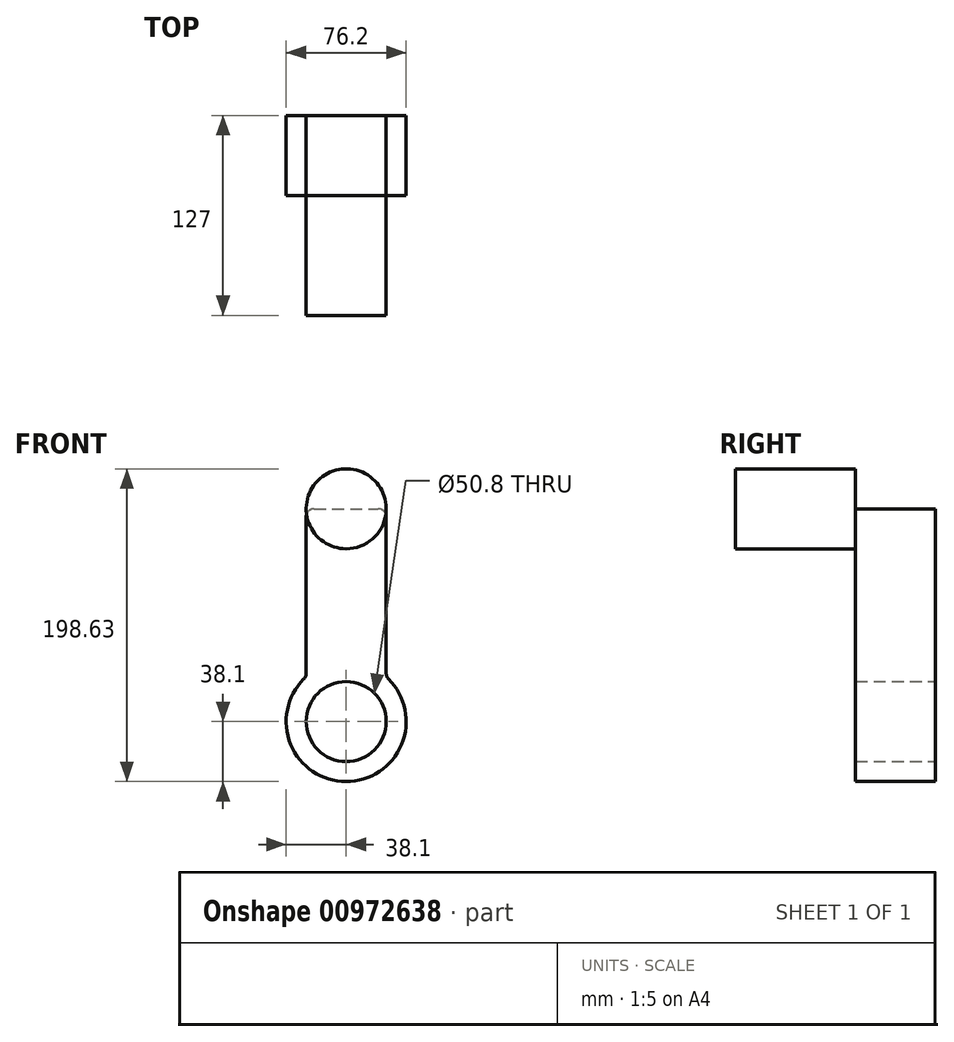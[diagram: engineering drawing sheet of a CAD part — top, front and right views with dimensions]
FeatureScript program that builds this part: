
annotation { "Feature Type Name" : "Feature", "Feature Type Description" : "" }
export const myFeature = defineFeature(function(context is Context, id is Id, definition is map)
    precondition{}
    {
        {
            var Q0;
            Q0=qCreatedBy(makeId("Front.planeOp"),FACE);
            var sketch = newSketch(context, id + "F0", { "sketchPlane" : qUnion([Q0])});
            skCircle(sketch, "E0", {"center": v(0, 0) * mm, "radius": 25.4 * mm});
            skCircle(sketch, "E1", {"center": v(0, 0) * mm, "radius": 38.1 * mm});
            skLineSegment(sketch, "E2.bottom", {"start": v(-18.1, 33.53) * mm, "end": v(18.4, 33.53) * mm});
            skLineSegment(sketch, "E2.top", {"start": v(-18.1, 135.13) * mm, "end": v(18.4, 135.13) * mm});
            skLineSegment(sketch, "E2.left", {"start": v(-18.1, 33.53) * mm, "end": v(-18.1, 135.13) * mm});
            skLineSegment(sketch, "E2.right", {"start": v(18.4, 33.53) * mm, "end": v(18.4, 135.13) * mm});
            skCircle(sketch, "E3", {"center": v(0, 135.13) * mm, "radius": 25.4 * mm});
            skLineSegment(sketch, "E4.bottom", {"start": v(-25.4, 135.13) * mm, "end": v(25.46, 135.13) * mm});
            skLineSegment(sketch, "E4.top", {"start": v(-25.4, 28.34) * mm, "end": v(25.46, 28.34) * mm});
            skLineSegment(sketch, "E4.left", {"start": v(-25.4, 135.13) * mm, "end": v(-25.4, 28.34) * mm});
            skLineSegment(sketch, "E4.right", {"start": v(25.46, 135.13) * mm, "end": v(25.46, 28.34) * mm});
            skSolve(sketch);
        }
        {
            var Q0;
            {var subQ0=sQuery(id+"F0.wireOp",EDGE,"E4.bottom");var subQ1=sQuery(id+"F0.wireOp",EDGE,"E2.left");var subQ2=makeQuery(id+"F0.imprint","INTERSECT",VERTEX,{"derivedFrom":[subQ1,subQ0]});Q0=makeQuery(id+"F0.imprint","IMPRINT",FACE,{"disambiguationData":[TD([[makeQuery(id+"F0.imprint","IMPRINT",EDGE,{"disambiguationData":[TD([[subQ2,1.0]])],"derivedFrom":subQ1}),-1.0]])]});}
            var Q1;
            {var subQ0=sQuery(id+"F0.wireOp",EDGE,"E4.bottom");var subQ4=makeQuery(id+"F0.imprint","INTERSECT",VERTEX,{"derivedFrom":[sQuery(id+"F0.wireOp",EDGE,"E2.left"),subQ0]});Q1=makeQuery(id+"F0.imprint","IMPRINT",FACE,{"disambiguationData":[TD([[makeQuery(id+"F0.imprint","IMPRINT",EDGE,{"disambiguationData":[TD([[subQ4,-1.0]])],"derivedFrom":subQ0}),1.0]])]});}
            var Q2;
            {var subQ0=sQuery(id+"F0.wireOp",EDGE,"E4.bottom");var subQ1=sQuery(id+"F0.wireOp",EDGE,"E2.left");var subQ2=makeQuery(id+"F0.imprint","INTERSECT",VERTEX,{"derivedFrom":[subQ1,subQ0]});Q2=makeQuery(id+"F0.imprint","IMPRINT",FACE,{"disambiguationData":[TD([[makeQuery(id+"F0.imprint","IMPRINT",EDGE,{"disambiguationData":[TD([[subQ2,1.0]])],"derivedFrom":subQ1}),1.0]])]});}
            var Q3;
            {var subQ0=sQuery(id+"F0.wireOp",EDGE,"E4.bottom");var subQ1=sQuery(id+"F0.wireOp",EDGE,"E2.right");var subQ2=makeQuery(id+"F0.imprint","INTERSECT",VERTEX,{"derivedFrom":[subQ1,subQ0]});Q3=makeQuery(id+"F0.imprint","IMPRINT",FACE,{"disambiguationData":[TD([[makeQuery(id+"F0.imprint","IMPRINT",EDGE,{"disambiguationData":[TD([[subQ2,1.0]])],"derivedFrom":subQ1}),-1.0]])]});}
            var Q4;
            {var subQ0=sQuery(id+"F0.wireOp",EDGE,"E2.right");var subQ1=sQuery(id+"F0.wireOp",EDGE,"E2.bottom");var subQ2=makeQuery(id+"F0.imprint","INTERSECT",VERTEX,{"derivedFrom":[subQ1,subQ0]});Q4=makeQuery(id+"F0.imprint","IMPRINT",FACE,{"disambiguationData":[TD([[makeQuery(id+"F0.imprint","IMPRINT",EDGE,{"disambiguationData":[TD([[subQ2,1.0]])],"derivedFrom":subQ1}),1.0]])]});}
            var Q5;
            {var subQ1=sQuery(id+"F0.wireOp",EDGE,"E1");var subQ3=sQuery(id+"F0.wireOp",EDGE,"E4.left");var subQ4=makeQuery(id+"F0.imprint","INTERSECT",VERTEX,{"derivedFrom":[subQ1,subQ3]});Q5=makeQuery(id+"F0.imprint","IMPRINT",FACE,{"disambiguationData":[TD([[makeQuery(id+"F0.imprint","IMPRINT",EDGE,{"disambiguationData":[TD([[subQ4,1.0]])],"derivedFrom":subQ1}),-1.0]])]});}
            var Q6;
            {var subQ9=sQuery(id+"F0.wireOp",EDGE,"E4.right");Q6=makeQuery(id+"F0.imprint","IMPRINT",FACE,{"disambiguationData":[TD([[makeQuery(id+"F0.imprint","IMPRINT",EDGE,{"derivedFrom":subQ9}),-1.0]])]});}
            var Q7;
            {var subQ0=sQuery(id+"F0.wireOp",EDGE,"E2.bottom");var subQ1=sQuery(id+"F0.wireOp",EDGE,"E1");var subQ3=makeQuery(id+"F0.imprint","INTERSECT",VERTEX,{"derivedFrom":[subQ1,subQ0]});Q7=makeQuery(id+"F0.imprint","IMPRINT",FACE,{"disambiguationData":[TD([[makeQuery(id+"F0.imprint","IMPRINT",EDGE,{"disambiguationData":[TD([[subQ3,-1.0]])],"derivedFrom":subQ1}),1.0]])]});}
            var Q8;
            Q8=makeQuery(id+"F0.imprint","IMPRINT",FACE,{"disambiguationData":[TD([[makeQuery(id+"F0.imprint","IMPRINT",EDGE,{"derivedFrom":sQuery(id+"F0.wireOp",EDGE,"E0")}),-1.0]])]});
            var Q9;
            {var subQ0=sQuery(id+"F0.wireOp",EDGE,"E4.top");Q9=makeQuery(id+"F0.imprint","IMPRINT",FACE,{"disambiguationData":[TD([[makeQuery(id+"F0.imprint","IMPRINT",EDGE,{"derivedFrom":subQ0}),1.0]])]});}
            extrude(context, id + "F1", {"entities" : qUnion([Q0, Q1, Q2, Q3, Q4, Q5, Q6, Q7, Q8, Q9]), "depth" : 76.2 * mm, "offsetDistance" : 25.4 * mm});
        }
        {
            var Q0;
            Q0=makeQuery(id+"F1.opExtrude","CAP_FACE",FACE,{"disambiguationData":[OSD([sQuery(id+"F0.wireOp",EDGE,"E0"),sQuery(id+"F0.wireOp",EDGE,"E1"),sQuery(id+"F0.wireOp",EDGE,"E3"),sQuery(id+"F0.wireOp",EDGE,"E4.bottom"),sQuery(id+"F0.wireOp",EDGE,"E4.left"),sQuery(id+"F0.wireOp",EDGE,"E4.right")])],"isStart":false});
            var sketch = newSketch(context, id + "F2", { "sketchPlane" : qUnion([Q0])});
            skLineSegment(sketch, "E5", {"start": v(25.46, 135.13) * mm, "end": v(-25.4, 135.13) * mm});
            skCircle(sketch, "E6", {"center": v(0.03, 135.13) * mm, "radius": 25.4 * mm});
            skSolve(sketch);
        }
        {
            var Q0;
            {var subQ0=sQuery(id+"F2.wireOp",EDGE,"E5");var subQ3=sQuery(id+"F2.wireOp",EDGE,"E6");var subQ4=makeQuery(id+"F2.imprint","INTERSECT",VERTEX,{"disambiguationData":[OD(1.0)],"derivedFrom":[subQ0,subQ3]});Q0=makeQuery(id+"F2.imprint","IMPRINT",FACE,{"disambiguationData":[TD([[makeQuery(id+"F2.imprint","IMPRINT",EDGE,{"disambiguationData":[TD([[subQ4,1.0]])],"derivedFrom":subQ0}),-1.0]])]});}
            var Q1;
            {var subQ0=sQuery(id+"F2.wireOp",EDGE,"E5");var subQ2=sQuery(id+"F2.wireOp",EDGE,"E6");var subQ3=makeQuery(id+"F2.imprint","INTERSECT",VERTEX,{"disambiguationData":[OD(1.0)],"derivedFrom":[subQ0,subQ2]});Q1=makeQuery(id+"F2.imprint","IMPRINT",FACE,{"disambiguationData":[TD([[makeQuery(id+"F2.imprint","IMPRINT",EDGE,{"disambiguationData":[TD([[subQ3,1.0]])],"derivedFrom":subQ0}),1.0]])]});}
            extrude(context, id + "F3", {"entities" : qUnion([Q0, Q1]), "operationType" : NewBodyOperationType.ADD, "depth" : 76.2 * mm, "offsetDistance" : 25.4 * mm});
        }
        {
            var Q0;
            Q0=makeQuery(id+"F1.opExtrude","CAP_FACE",FACE,{"disambiguationData":[OSD([sQuery(id+"F0.wireOp",EDGE,"E0"),sQuery(id+"F0.wireOp",EDGE,"E1"),sQuery(id+"F0.wireOp",EDGE,"E3"),sQuery(id+"F0.wireOp",EDGE,"E4.bottom"),sQuery(id+"F0.wireOp",EDGE,"E4.left"),sQuery(id+"F0.wireOp",EDGE,"E4.right")])],"isStart":true});
            extrude(context, id + "F4", {"entities" : qUnion([Q0]), "operationType" : NewBodyOperationType.REMOVE, "oppositeDirection" : true, "depth" : 25.4 * mm, "offsetDistance" : 25.4 * mm});
        }
        {
            var Q0;
            Q0=makeQuery(id+"F1.opExtrude","SWEPT_EDGE",EDGE,{"disambiguationData":[OSD([sQuery(id+"F0.wireOp",EDGE,"E3"),sQuery(id+"F0.wireOp",EDGE,"E4.bottom"),sQuery(id+"F0.wireOp",EDGE,"E4.left")])]});
            var Q1;
            Q1=makeQuery(id+"F1.opExtrude","SWEPT_EDGE",EDGE,{"disambiguationData":[OSD([sQuery(id+"F0.wireOp",EDGE,"E1"),sQuery(id+"F0.wireOp",EDGE,"E4.left")])]});
            var Q2;
            Q2=makeQuery(id+"F1.opExtrude","SWEPT_EDGE",EDGE,{"disambiguationData":[OSD([sQuery(id+"F0.wireOp",EDGE,"E1"),sQuery(id+"F0.wireOp",EDGE,"E4.top"),sQuery(id+"F0.wireOp",EDGE,"E4.right")])]});
            var Q3;
            Q3=makeQuery(id+"F1.opExtrude","SWEPT_EDGE",EDGE,{"disambiguationData":[OSD([sQuery(id+"F0.wireOp",EDGE,"E4.bottom"),sQuery(id+"F0.wireOp",EDGE,"E4.right")])]});
            fillet(context, id + "F5", {"entities" : qUnion([Q0, Q1, Q2, Q3]), "radius" : 5.08 * mm, "tangentPropagation" : true, "allowEdgeOverflow" : false});
        }
    });
